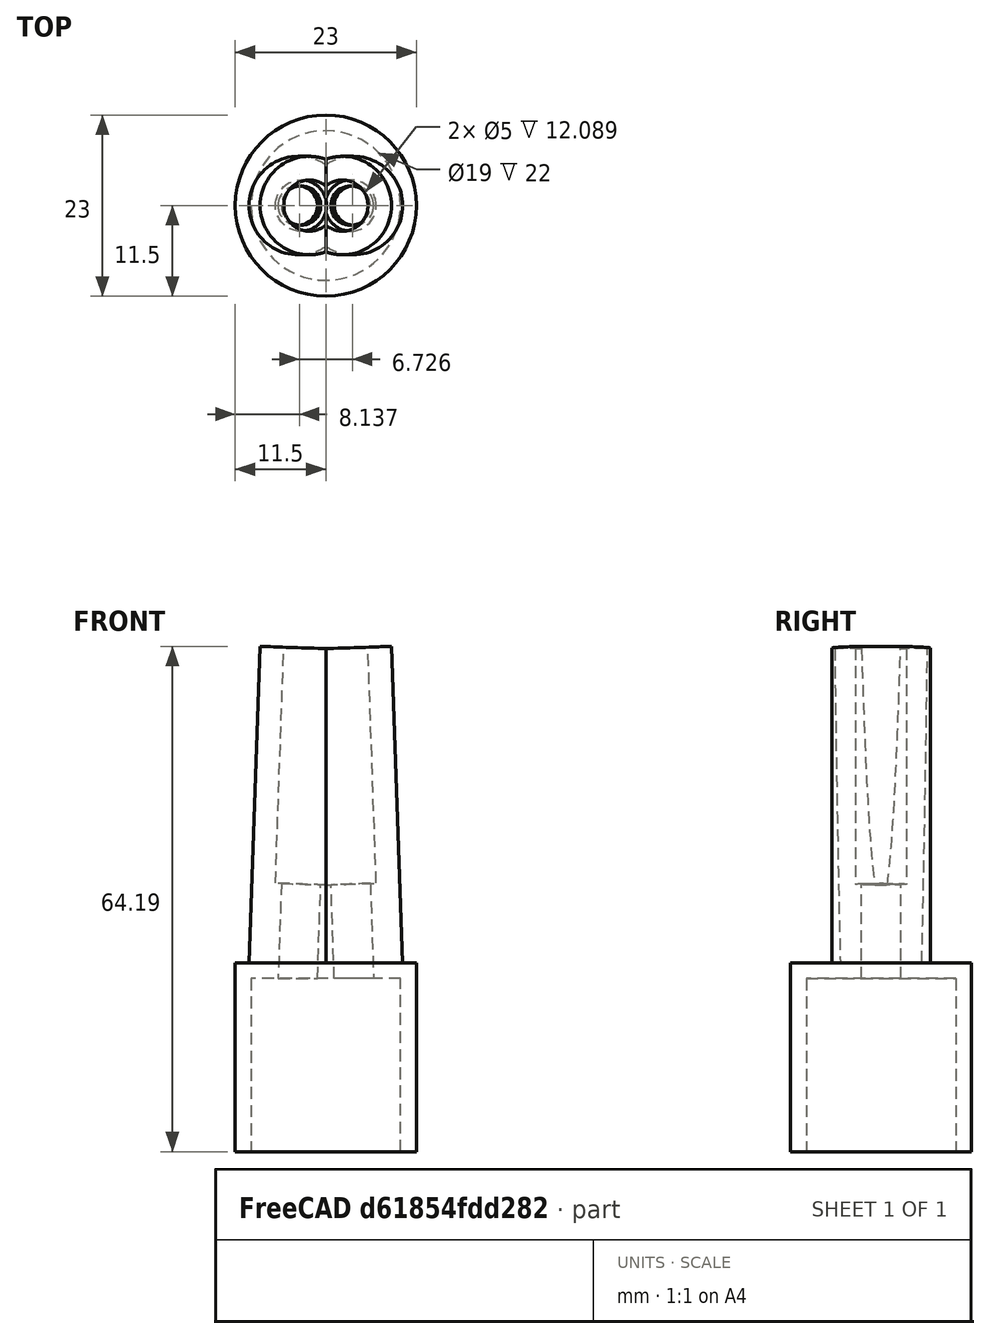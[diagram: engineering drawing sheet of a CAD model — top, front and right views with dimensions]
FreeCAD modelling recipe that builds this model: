
FCSTD DOCUMENT  (FreeCAD 0.19R24366 (Git))
Label: Датчик препятствий насадка
License: All rights reserved
LicenseURL: http://en.wikipedia.org/wiki/All_rights_reserved
objects: Sketcher::SketchObject×5, PartDesign::Pad×3, PartDesign::Mirrored×2, PartDesign::Pocket×2, Mesh::Feature×1, PartDesign::CoordinateSystem×1, PartDesign::Plane×1, PartDesign::Body×1
note: 20 computed .brp shape members not serialized (recipe doc carries the construction recipe); baked Part::Feature solids carry a one-line shape summary decoded from their .brp

FEATURE [Mesh::Feature] ___________________________________________________3  label="Датчик препятствий насадка 3"
FEATURE [Sketcher::SketchObject] Sketch
  FullyConstrained = true
  MapMode = 5
  Support = -> [XY_Plane]
  sketch-geometry (2):
    g0: Circle CenterX=0 CenterY=0 CenterZ=0 NormalX=0 NormalY=0 NormalZ=1 AngleXU=0 Radius=11.5
    g1: Circle CenterX=0 CenterY=0 CenterZ=0 NormalX=0 NormalY=0 NormalZ=1 AngleXU=0 Radius=9.5
  constraints (4):
    c: Coincident(g0,g-1)
    c: Coincident(g1,g0)
    c: Diameter(g1) = 19
    c: Diameter(g0) = 23
FEATURE [Sketcher::SketchObject] Sketch001
  AttachmentOffset = pos=(0,0,22) rot=(0,0,1;0rad)
  FullyConstrained = true
  MapMode = 5
  Placement = pos=(0,0,22) rot=(0,0,1;0rad)
  Support = -> [XY_Plane]
  expr: .AttachmentOffset.Base.z = Pad.Length
  sketch-geometry (1):
    g0: Circle CenterX=0 CenterY=0 CenterZ=0 NormalX=0 NormalY=0 NormalZ=1 AngleXU=0 Radius=11.5
  constraints (2):
    c: Coincident(g0,g-1)
    c: Diameter(g0) = 23
FEATURE [PartDesign::Pad] Pad
  Direction = (1,1,1)
  Length = 22
  Length2 = 100
  Profile = -> Sketch
  Type = 0
FEATURE [PartDesign::Pad] Pad001
  BaseFeature = -> Pad
  Direction = (1,1,1)
  Length = 2
  Length2 = 100
  Profile = -> Sketch001
  Type = 0
FEATURE [PartDesign::CoordinateSystem] Local_CS
  AttacherType = Attacher::AttachEngine3D
  AttachmentOffset = pos=(3.5,0,24) rot=(0,-1,0;0.034986rad)
  MapMode = 5
  Placement = pos=(3.5,0,24) rot=(0,-1,0;0.034986rad)
  Support = -> [XY_Plane]
  expr: .AttachmentOffset.Rotation.Pitch = -atan(3.5 / 100)
  expr: .AttachmentOffset.Base.z = Pad.Length + Pad001.Length
FEATURE [PartDesign::Plane] DatumPlane
  Length = 63.3936
  MapMode = 5
  Placement = pos=(3.5,0,24) rot=(0,-1,0;0.034986rad)
  ResizeMode = 0
  Support = -> [Local_CS]
  Width = 60.3043
FEATURE [Sketcher::SketchObject] Sketch007
  FullyConstrained = true
  MapMode = 5
  Placement = pos=(3.5,0,24) rot=(0,-1,0;0.034986rad)
  Support = -> [DatumPlane]
  sketch-geometry (1):
    g0: Circle CenterX=0 CenterY=0 CenterZ=0 NormalX=0 NormalY=0 NormalZ=1 AngleXU=0 Radius=2.5
  constraints (2):
    c: Coincident(g0,g-1)
    c: Diameter(g0) = 5
FEATURE [Sketcher::SketchObject] Sketch008
  AttachmentOffset = pos=(0,0,10) rot=(0,0,1;0rad)
  FullyConstrained = true
  MapMode = 5
  Placement = pos=(3.15021,0,33.9939) rot=(0,-1,0;0.034986rad)
  Support = -> [DatumPlane]
  sketch-geometry (1):
    g0: Circle CenterX=0 CenterY=0 CenterZ=0 NormalX=0 NormalY=0 NormalZ=1 AngleXU=0 Radius=3.25
  constraints (2):
    c: Coincident(g0,g-1)
    c: Diameter(g0) = 6.5
FEATURE [Sketcher::SketchObject] Sketch009
  FullyConstrained = true
  MapMode = 5
  Placement = pos=(3.5,0,24) rot=(0,-1,0;0.034986rad)
  Support = -> [DatumPlane]
  expr: Constraints[1] = Sketch008.Constraints[1] + 6mm
  sketch-geometry (1):
    g0: Circle CenterX=0 CenterY=0 CenterZ=0 NormalX=0 NormalY=0 NormalZ=1 AngleXU=0 Radius=6.25
  constraints (2):
    c: Coincident(g0,g-1)
    c: Diameter(g0) = 12.5
FEATURE [PartDesign::Pad] Pad002
  BaseFeature = -> Pad001
  Direction = (1,1,1)
  Length = 40
  Length2 = 1
  Profile = -> Sketch009
  Type = 4
FEATURE [PartDesign::Mirrored] Mirrored
  BaseFeature = -> Pad002
  MirrorPlane = -> YZ_Plane
  Originals = -> [Pad002]
FEATURE [PartDesign::Pocket] Pocket
  BaseFeature = -> Mirrored
  Length = 5
  Length2 = 100
  Midplane = true
  Profile = -> Sketch007
  Type = 1
FEATURE [PartDesign::Pocket] Pocket001
  BaseFeature = -> Pocket
  Length = 5
  Length2 = 100
  Profile = -> Sketch008
  Reversed = true
  Type = 1
FEATURE [PartDesign::Mirrored] Mirrored001
  BaseFeature = -> Pocket001
  MirrorPlane = -> YZ_Plane
  Originals = -> [Pocket,Pocket001]
FEATURE [PartDesign::Body] Body
  Group = -> [Sketch,Sketch001,Pad,Pad001,Local_CS,DatumPlane,Sketch007,Sketch008,Sketch009,Pad002,Mirrored,Pocket,Pocket001,Mirrored001]
  Origin = -> Origin
  Tip = -> Mirrored001
